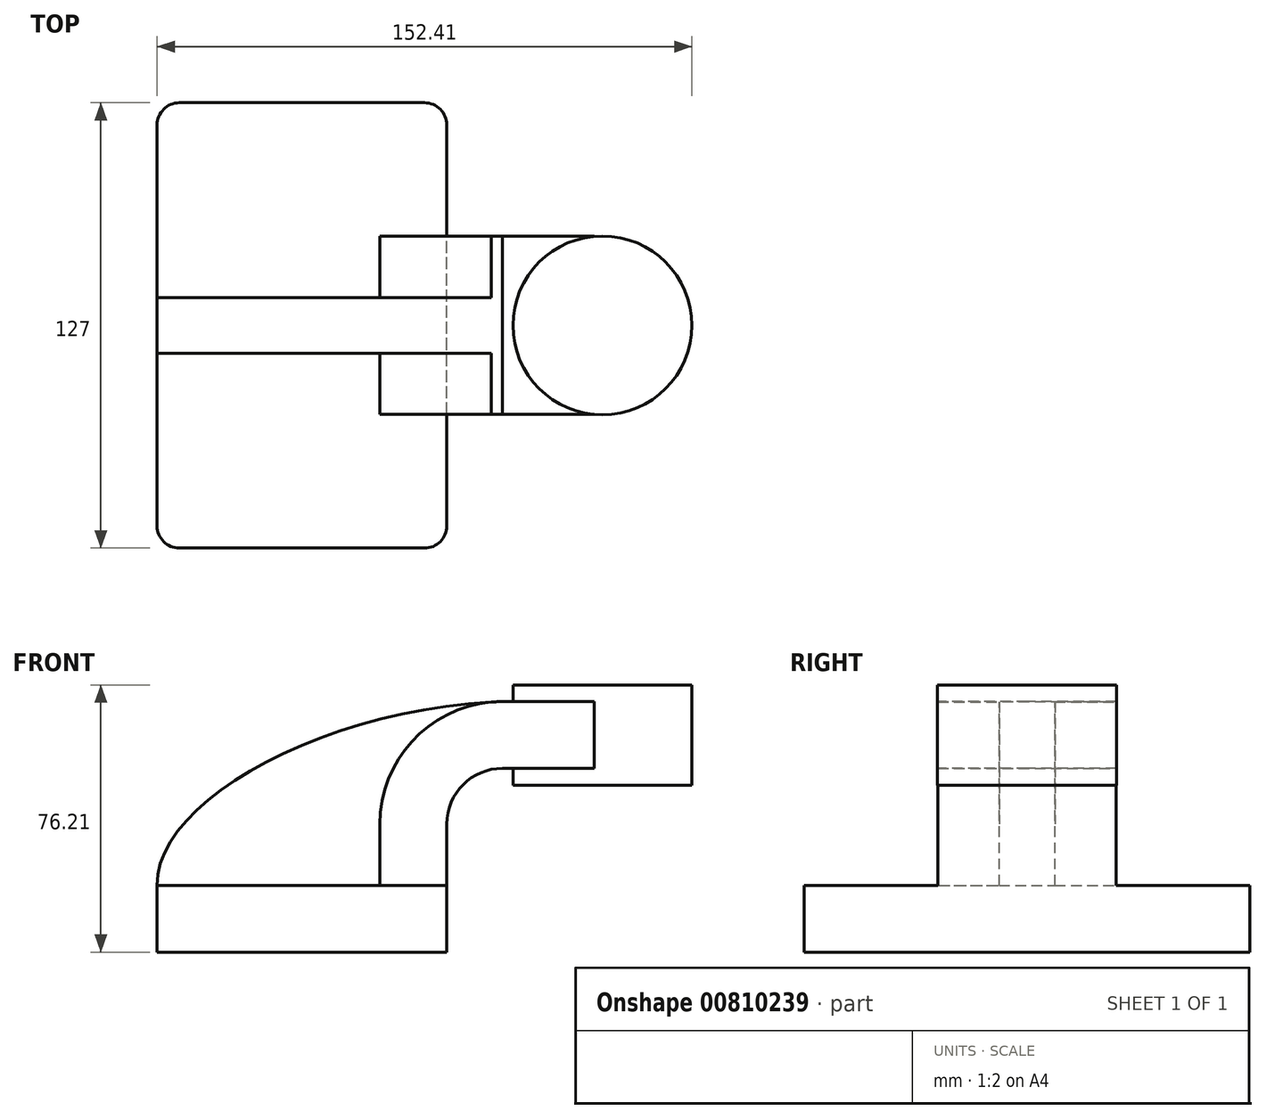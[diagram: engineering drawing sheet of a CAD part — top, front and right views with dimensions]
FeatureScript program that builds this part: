
annotation { "Feature Type Name" : "Feature", "Feature Type Description" : "" }
export const myFeature = defineFeature(function(context is Context, id is Id, definition is map)
    precondition{}
    {
        {
            var Q0;
            Q0=qCreatedBy(makeId("Front.planeOp"),FACE);
            var sketch = newSketch(context, id + "F0", { "sketchPlane" : qUnion([Q0])});
            skLineSegment(sketch, "E0.bottom", {"start": v(41.28, -9.52) * mm, "end": v(-41.28, -9.53) * mm});
            skLineSegment(sketch, "E0.top", {"start": v(41.28, 9.53) * mm, "end": v(-41.28, 9.53) * mm});
            skLineSegment(sketch, "E0.left", {"start": v(41.28, -9.52) * mm, "end": v(41.28, 9.53) * mm});
            skLineSegment(sketch, "E0.right", {"start": v(-41.28, -9.53) * mm, "end": v(-41.28, 9.53) * mm});
            skPoint(sketch, "E0.middle", {"position": v(0, 0) * mm});
            skLineSegment(sketch, "E1.bottom", {"start": v(111.12, 38.1) * mm, "end": v(60.32, 38.1) * mm});
            skLineSegment(sketch, "E1.top", {"start": v(111.12, 66.68) * mm, "end": v(60.32, 66.68) * mm});
            skLineSegment(sketch, "E1.left", {"start": v(111.12, 38.1) * mm, "end": v(111.12, 66.68) * mm});
            skLineSegment(sketch, "E1.right", {"start": v(60.32, 38.1) * mm, "end": v(60.32, 66.68) * mm});
            skPoint(sketch, "E1.middle", {"position": v(85.72, 52.39) * mm});
            skLineSegment(sketch, "E2", {"start": v(41.28, 9.53) * mm, "end": v(41.28, 27) * mm});
            skArc(sketch, "E3", {"start": v(41.27, 27) * mm, "mid": v(45.92, 38.23) * mm, "end": v(57.15, 42.88) * mm});
            skLineSegment(sketch, "E4", {"start": v(57.15, 42.88) * mm, "end": v(85.62, 42.88) * mm});
            skLineSegment(sketch, "E5.0", {"start": v(57.15, 61.93) * mm, "end": v(85.62, 61.93) * mm});
            skArc(sketch, "E5.1", {"start": v(22.23, 27) * mm, "mid": v(32.45, 51.7) * mm, "end": v(57.15, 61.93) * mm});
            skLineSegment(sketch, "E5.2", {"start": v(22.22, 9.53) * mm, "end": v(22.22, 27) * mm});
            skLineSegment(sketch, "E6", {"start": v(85.62, 38.1) * mm, "end": v(85.62, 66.68) * mm});
            skPoint(sketch, "E6.startSnap0", {"position": v(85.72, 38.1) * mm});
            skFitSpline(sketch, "E7", {"points": [v(-41.28, 9.53) * mm, v(57.15, 61.93) * mm], "startDerivative": vector(-1.33, 71.95) * mm, "endDerivative": vector(153.24, 5.6) * mm});
            skSolve(sketch);
        }
        {
            var Q0;
            Q0=makeQuery(id+"F0.imprint","IMPRINT",FACE,{"disambiguationData":[TD([[makeQuery(id+"F0.imprint","IMPRINT",EDGE,{"derivedFrom":sQuery(id+"F0.wireOp",EDGE,"E0.bottom")}),-1.0]])]});
            extrude(context, id + "F1", {"entities" : qUnion([Q0]), "endBound" : BoundingType.SYMMETRIC, "depth" : 127 * mm, "offsetDistance" : 25.4 * mm});
        }
        {
            var Q0;
            {var subQ1=sQuery(id+"F0.wireOp",EDGE,"E2");Q0=makeQuery(id+"F0.imprint","IMPRINT",FACE,{"disambiguationData":[TD([[makeQuery(id+"F0.imprint","IMPRINT",EDGE,{"derivedFrom":subQ1}),1.0]])]});}
            var Q1;
            {var subQ0=sQuery(id+"F0.wireOp",EDGE,"E4");var subQ1=sQuery(id+"F0.wireOp",EDGE,"E1.right");var subQ2=makeQuery(id+"F0.imprint","INTERSECT",VERTEX,{"derivedFrom":[subQ1,subQ0]});Q1=makeQuery(id+"F0.imprint","IMPRINT",FACE,{"disambiguationData":[TD([[makeQuery(id+"F0.imprint","IMPRINT",EDGE,{"disambiguationData":[TD([[subQ2,-1.0]])],"derivedFrom":subQ1}),-1.0]])]});}
            extrude(context, id + "F2", {"entities" : qUnion([Q0, Q1]), "operationType" : NewBodyOperationType.ADD, "endBound" : BoundingType.SYMMETRIC, "depth" : 50.8 * mm, "offsetDistance" : 25.4 * mm});
        }
        {
            var Q0;
            {var subQ3=sQuery(id+"F0.wireOp",EDGE,"E5.2");Q0=makeQuery(id+"F0.imprint","IMPRINT",FACE,{"disambiguationData":[TD([[makeQuery(id+"F0.imprint","IMPRINT",EDGE,{"derivedFrom":subQ3}),1.0]])]});}
            extrude(context, id + "F3", {"entities" : qUnion([Q0]), "operationType" : NewBodyOperationType.ADD, "endBound" : BoundingType.SYMMETRIC, "depth" : 15.88 * mm, "offsetDistance" : 25.4 * mm});
        }
        {
            var Q0;
            {var subQ0=sQuery(id+"F0.wireOp",EDGE,"E1.left");Q0=makeQuery(id+"F0.imprint","IMPRINT",FACE,{"disambiguationData":[TD([[makeQuery(id+"F0.imprint","IMPRINT",EDGE,{"derivedFrom":subQ0}),1.0]])]});}
            var Q1;
            Q1=sQuery(id+"F0.wireOp",EDGE,"E6");
            revolve(context, id + "F4", {"operationType" : NewBodyOperationType.ADD, "surfaceOperationType" : NewSurfaceOperationType.NEW, "entities" : qUnion([Q0]), "axis" : qUnion([Q1]), "revolveType" : RevolveType.FULL});
        }
        {
            var Q0;
            Q0=makeQuery(id+"F1.opExtrude","CAP_EDGE",EDGE,{"disambiguationData":[OSD([sQuery(id+"F0.wireOp",EDGE,"E0.left")])],"isStart":false});
            var Q1;
            Q1=makeQuery(id+"F1.opExtrude","CAP_EDGE",EDGE,{"disambiguationData":[OSD([sQuery(id+"F0.wireOp",EDGE,"E0.left")])],"isStart":true});
            var Q2;
            Q2=makeQuery(id+"F1.opExtrude","CAP_EDGE",EDGE,{"disambiguationData":[OSD([sQuery(id+"F0.wireOp",EDGE,"E0.right")])],"isStart":true});
            var Q3;
            Q3=makeQuery(id+"F1.opExtrude","CAP_EDGE",EDGE,{"disambiguationData":[OSD([sQuery(id+"F0.wireOp",EDGE,"E0.right")])],"isStart":false});
            fillet(context, id + "F5", {"entities" : qUnion([Q0, Q1, Q2, Q3]), "radius" : 6.35 * mm, "tangentPropagation" : true, "allowEdgeOverflow" : false});
        }
    });
